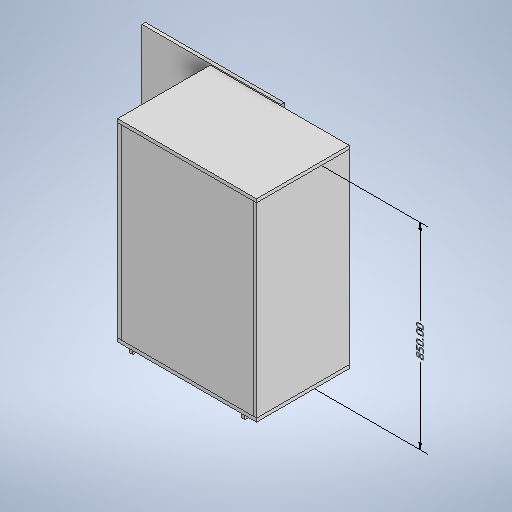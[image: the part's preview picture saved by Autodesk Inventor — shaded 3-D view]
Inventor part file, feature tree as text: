
AUTODESK INVENTOR PART (.ipt)
format: ipt  version: 2025.3 (Build 293356000, 356)  size: 456,192 bytes
history: native  units: mm
features: other x18, sketch x13, extrude x10, mirror x2, pattern_linear x1, move_body x1
ambient origin geometry x8: Origin, YZ Plane, XZ Plane, XY Plane, X Axis, Y Axis, Z Axis, Center Point
bodies: Body1 (feature_tree), Body2 (feature_tree), Body3 (feature_tree), Body4 (feature_tree), Body5 (feature_tree), Body6 (feature_tree), Body7 (feature_tree), Body8 (feature_tree), Body9 (feature_tree), Body10 (feature_tree), Body11 (feature_tree), Body12 (feature_tree), Body13 (feature_tree)
feature tree (45):
  other  "Annotations"
  sketch  "Sketch1"  dims[d0=835.0mm d1=600.0mm d2=600.0mm]
  sketch  "Sketch2"  dims[d3=400.0mm d22=20.0mm d24=820.0mm]
  extrude  "Extrusion2"  Depth=600.0mm
  sketch  "Sketch5"  dims[d34=15.0mm d35=20.0mm d37=370.0mm]
  pattern_linear  "Rectangular Pattern1"  Count1=60  [1 undecoded]
  extrude  "Extrusion3"  Depth=20.0mm
  extrude  "Extrusion4"  Depth=15.0mm
  mirror  "Mirror1"
  extrude  "Extrusion5"  TaperAngle=0.0deg  [1 undecoded]
  extrude  "Extrusion6"  Depth=20.0mm
  mirror  "Mirror2"
  extrude  "Extrusion7"  Depth=15.0mm TaperAngle=0.0deg
  extrude  "Extrusion8"  Depth=15.0mm
  move_body  "Move Body1"
  extrude  "Extrusion9"  Depth=248.333333mm
  extrude  "Extrusion10"  Depth=15.0mm
  extrude  "Extrusion11"  Depth=15.0mm
  sketch  "Sketch4"  dims[d32=15.0mm d33=0.0mm]
  other  "ITEM1"
  sketch  "Sketch Rectangular Pattern2"  dims[d25=15.0mm d26=0.0mm d31=15.0mm]
  other  "Pattern of ITEM1:2"
  other  "ITEM1A"
  other  "ITEM6"
  sketch  "Sketch6"  dims[d38=20.0mm d40=555.0mm d43=15.0mm d44=0.0mm]
  other  "ITEM7"
  other  "Pattern of ITEM7:3"
  other  "ITEM7A"
  sketch  "Sketch7"  dims[d46=15.0mm d47=15.0mm]
  other  "ITEM8"
  sketch  "Sketch8"  dims[d49=15.0mm d52=248.333333mm]
  other  "ITEM2"
  other  "Pattern of ITEM2:4"
  other  "ITEM2A"
  sketch  "Sketch9"  dims[d53=248.333333mm d54=15.0mm]
  other  "ITEM3"
  sketch  "Sketch10"  dims[d55=10.0mm d56=0.0mm d57=15.0mm]
  other  "ITEM4"
  sketch  "Sketch11"  dims[d58=15.0mm]
  other  "ITEM5"
  sketch  "Sketch12"  dims[d59=0.0mm]
  other  "ITEM5A"
  sketch  "Sketch13"  dims[d60=15.0mm d61=15.0mm d62=0.0mm d63=10.0mm d64=0.0mm d65=15.0mm d66=15.0mm d67=248.333333mm d68=15.0mm d69=15.0mm d70=15.0mm d71=15.0mm d72=15.0mm d73=15.0mm d74=0.0mm d75=15.0mm d76=0.0mm d77=15.0mm d78=0.0mm d79=-300.0mm d80=0.0mm d81=-5.0mm d82=15.0mm d83=0.0mm d84=15.0mm d85=0.0mm d86=15.0mm d87=50.0mm d88=15.0mm d89=50.0mm d90=15.0mm d91=0.0mm d92=6.619503mm d93=7.932904mm d94=850.0mm]
  other  "ITEM9"
  other  "Linear Dimension 1"
note: 2 required parameter values undecoded (feature->parameter linkage not recoverable at this tier; creation-order binding heuristic only, values carry confidence <= 0.55)
